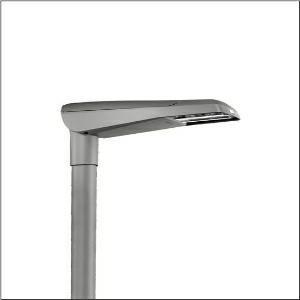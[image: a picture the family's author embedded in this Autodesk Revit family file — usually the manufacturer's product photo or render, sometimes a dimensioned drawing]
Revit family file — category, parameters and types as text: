
# Revit family: streetlight_sl_11_iq_micro___p1_0a_5xc1c41e08ce_7fd7
name_source: partatom
category: Lighting Fixtures
units: mm (PartAtom-declared; Revit-internal decimal feet)

## family parameters
Cut with Voids When Loaded = No
Host = Face
Light Source = No
Part Type = Normal
Room Calculation Point = No
Round Connector Dimension = Use Diameter
Shared = No

## types (1)
- --- (1 x LED, 1660 lm, 10.8 W, 4000K)
    Apparent Load = 11 VA
    CIE Flux Codes = 29 63 93 100 100
    Color Rendering = 70
    Color Temperature = 4000K
    Default Elevation = 1800 mm
    Description = Streetlight SL 11 iQ micro, mast luminaire, primary light control with 3 zone facetted reflector, of plastic, silver coated, highly specular, primary optical cover: cover, of PMMA, transparent, light distribution: P1.0a, light emission: direct distribution, primary light characteristic: asymmetric, installation type: post-top, side-entry, lamps: LED, High Power LED, rated values: 1.660lm | 10,8W | 153,7lm/W (begin service life); end service life: 1.660lm | 11,1W; at 50% lumin. flux: 830lm | 6W | 138,3lm/W, colour temperature: 4000K, colour rendering: CRI > 70, light colour: 740, light setting 1 begin service life: 100% | 1.660lm | 10,8W | 153,7lm/W | 4.000K, light setting 1 end service life: 11,1W, further light settings possible, control: optimised constant luminous flux control (CLO 2.0), Desk-Remote (wireless, voltage-free reading and setting of iQ features in the workshop via application-optimized NFC function/RFID function), Light-Fading, Smart-Wire, Night-Set, Lumen-Switch, Temp-Guard, Auto-Match, with cable H07RN-F 3x 1.5mm², mains connection: 230..240V, AC, 50/60Hz, connection cable pre-assembled, cable length: 5,5m, luminaire housing, of diecast aluminium, powder-coated, SITECO metallic grey (DB 702S), please order mast flange separately, inclination adjustable without tools: 0°, 5°, 10°, 15° (post-top) | 0°, -5°, -10°, -15° (side-entry), sealing non-destructively replaceable, multi-level sealing system, length: 600mm, width: 174mm, height: 116mm, mast flange for spigot size: 42mm (side-entry): 5XC10008XM4, 60/48mm (side-entry/post-top): 5XC10108XM2, 76/60mm (side-entry/post-top): 5XC10108XM1, equipment: standard, protection rating (complete): IP66, insulation class (complete): insulation class II (safety insulation), certification: CE, ENEC, ENEC+, VDE, impact resistance: IK10, permissible operating ambient temperature for outdoor applications: -25..+50°C, standard-compliant lighting for roads and squares, Environmental Product Declaration (EPD) tested and certified by an independent institute, packaging unit: 1 piece

Light Distribution: P1.0a
    Height = 116 mm
    Lamp = 1 x LED
    Lamp Light Flux = 1660 lm
    Lamp Power = 10.8 W
    Lamp count = 1
    Length = 600 mm
    Luminous efficacy = 154 lm/W
    Manufacturer = Siteco
    ModVariant = No
    Model = 5XC1C41E08CE
    Number of Poles = 1
    OnlyDefault = Yes
    Power Factor = 1
    Product Name = Streetlight SL 11 iQ micro | P1.0a
    Product group = mast luminaire | pylon top
    ProductGroupID = 6100
    Protection Class = Protection class II
    Protection Degree = IP 66
    RLX_Detail_Level = 1
    RLX_Emergency_Light_Flux = 0 lm
    RLX_Emergency_Type = 0
    RLX_Emergency_Type_DB = No
    RlxData = <blob elided: 26693 chars, md5=3765ac3b>
    Socket = socket
    Standby Power = 0 W
    System Light Flux = 1660 lm
    System Power = 11 W
    Type Comments = factory setting: luminous flux: 100 % | dim-lin: 254 | 194 mA
    Type Image = l_1006566.jpg
    URL = http://relux.com
    VarID = @adj_019339
    Voltage = 0 V
    Weight = 0.00 kg
    Width = 174 mm

## geometry (parser evidence)
native form markers: Blend x4, Sweep x11
no freeform markers — native parametric forms only
